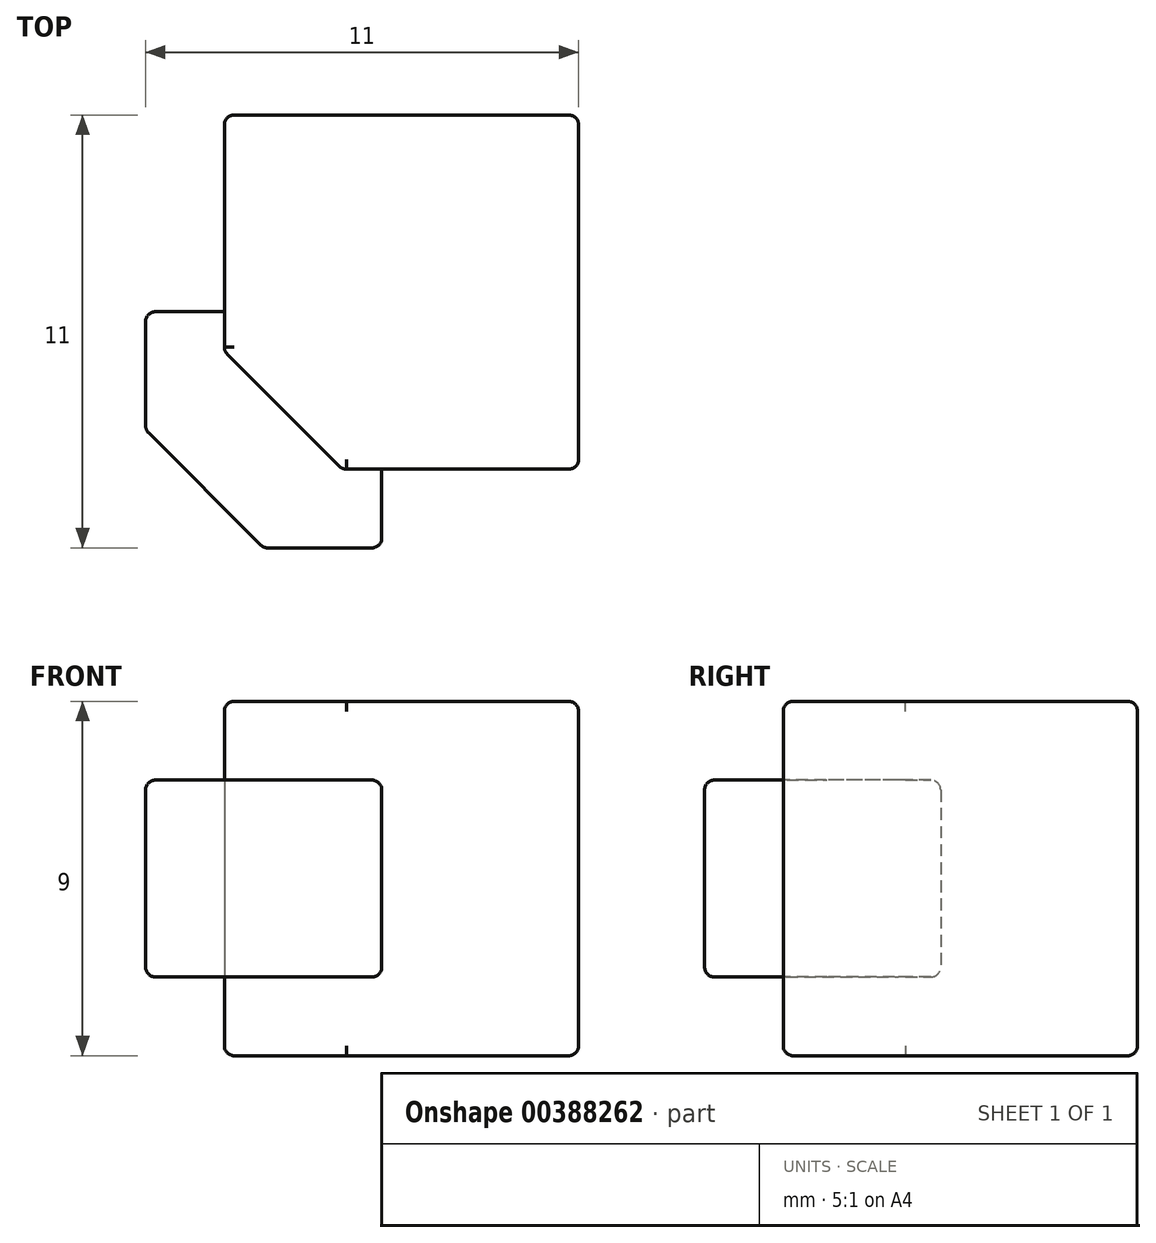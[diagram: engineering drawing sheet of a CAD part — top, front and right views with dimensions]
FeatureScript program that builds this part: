
annotation { "Feature Type Name" : "Feature", "Feature Type Description" : "" }
export const myFeature = defineFeature(function(context is Context, id is Id, definition is map)
    precondition{}
    {
        {
            var Q0;
            Q0=qCreatedBy(makeId("Top.planeOp"),FACE);
            var sketch = newSketch(context, id + "F0", { "sketchPlane" : qUnion([Q0])});
            skLineSegment(sketch, "E0.bottom", {"start": v(4.5, -4.5) * mm, "end": v(-4.5, -4.5) * mm});
            skLineSegment(sketch, "E0.top", {"start": v(4.5, 4.5) * mm, "end": v(-4.5, 4.5) * mm});
            skLineSegment(sketch, "E0.left", {"start": v(4.5, -4.5) * mm, "end": v(4.5, 4.5) * mm});
            skLineSegment(sketch, "E0.right", {"start": v(-4.5, -4.5) * mm, "end": v(-4.5, 4.5) * mm});
            skPoint(sketch, "E0.middle", {"position": v(0, 0) * mm});
            skSolve(sketch);
        }
        {
            var Q0;
            Q0 = qSketchRegion(id + "F0", true);
            extrude(context, id + "F1", {"entities" : qUnion([Q0]), "depth" : 9 * mm});
        }
        {
            var Q0;
            Q0=qCreatedBy(makeId("Top.planeOp"),FACE);
            var sketch = newSketch(context, id + "F2", { "sketchPlane" : qUnion([Q0])});
            skLineSegment(sketch, "E1.bottom", {"start": v(-6.5, -0.5) * mm, "end": v(-0.5, -0.5) * mm});
            skLineSegment(sketch, "E1.top", {"start": v(-6.5, -6.5) * mm, "end": v(-0.5, -6.5) * mm});
            skLineSegment(sketch, "E1.left", {"start": v(-6.5, -0.5) * mm, "end": v(-6.5, -6.5) * mm});
            skLineSegment(sketch, "E1.right", {"start": v(-0.5, -0.5) * mm, "end": v(-0.5, -6.5) * mm});
            skSolve(sketch);
        }
        {
            var Q0;
            Q0=makeQuery(id+"F2.imprint","IMPRINT",FACE,{"disambiguationData":[TD([[makeQuery(id+"F2.imprint","IMPRINT",EDGE,{"derivedFrom":sQuery(id+"F2.wireOp",EDGE,"E1.bottom")}),-1.0]])]});
            extrude(context, id + "F3", {"entities" : qUnion([Q0]), "operationType" : NewBodyOperationType.ADD, "depth" : 7 * mm, "hasSecondDirection" : true, "secondDirectionOppositeDirection" : false, "secondDirectionDepth" : 2 * mm});
        }
        {
            var Q0;
            {var subQ0=sQuery(id+"F0.wireOp",EDGE,"E0.bottom");var subQ1=sQuery(id+"F0.wireOp",EDGE,"E0.right");Q0=makeQuery(id+"F3.boolean.opBoolean","SPLIT",EDGE,{"disambiguationData":[TD([makeQuery(id+"F1.opExtrude","CAP_FACE",FACE,{"disambiguationData":[OSD([subQ0,sQuery(id+"F0.wireOp",EDGE,"E0.top"),sQuery(id+"F0.wireOp",EDGE,"E0.left"),subQ1])],"isStart":true})])],"derivedFrom":makeQuery(id+"F1.opExtrude","SWEPT_EDGE",EDGE,{"disambiguationData":[OSD([subQ0,subQ1])]})});}
            chamfer(context, id + "F4", {"entities" : qUnion([Q0]), "width" : 3 * mm, "tangentPropagation" : true});
        }
        {
            var Q0;
            Q0=makeQuery(id+"F3.opExtrude","SWEPT_EDGE",EDGE,{"disambiguationData":[OSD([sQuery(id+"F2.wireOp",EDGE,"E1.top"),sQuery(id+"F2.wireOp",EDGE,"E1.left")])]});
            chamfer(context, id + "F5", {"entities" : qUnion([Q0]), "width" : 3 * mm, "tangentPropagation" : true});
        }
        {
            var Q0;
            {var subQ0=sQuery(id+"F0.wireOp",EDGE,"E0.bottom");var subQ1=sQuery(id+"F0.wireOp",EDGE,"E0.right");Q0=makeQuery(id+"F3.boolean.opBoolean","SPLIT",EDGE,{"disambiguationData":[TD([makeQuery(id+"F1.opExtrude","CAP_FACE",FACE,{"disambiguationData":[OSD([subQ0,sQuery(id+"F0.wireOp",EDGE,"E0.top"),sQuery(id+"F0.wireOp",EDGE,"E0.left"),subQ1])],"isStart":false})])],"derivedFrom":makeQuery(id+"F1.opExtrude","SWEPT_EDGE",EDGE,{"disambiguationData":[OSD([subQ0,subQ1])]})});}
            chamfer(context, id + "F6", {"entities" : qUnion([Q0]), "width" : 3 * mm, "tangentPropagation" : true});
        }
        {
            var Q0;
            Q0=makeQuery(id+"F1.opExtrude","CAP_EDGE",EDGE,{"disambiguationData":[OSD([sQuery(id+"F0.wireOp",EDGE,"E0.right")])],"isStart":false});
            var Q1;
            Q1=makeQuery(id+"F1.opExtrude","CAP_EDGE",EDGE,{"disambiguationData":[OSD([sQuery(id+"F0.wireOp",EDGE,"E0.top")])],"isStart":false});
            var Q2;
            Q2=makeQuery(id+"F1.opExtrude","CAP_EDGE",EDGE,{"disambiguationData":[OSD([sQuery(id+"F0.wireOp",EDGE,"E0.left")])],"isStart":false});
            var Q3;
            Q3=makeQuery(id+"F1.opExtrude","CAP_EDGE",EDGE,{"disambiguationData":[OSD([sQuery(id+"F0.wireOp",EDGE,"E0.bottom")])],"isStart":false});
            var Q4;
            Q4=makeQuery(id+"F1.opExtrude","SWEPT_EDGE",EDGE,{"disambiguationData":[OSD([sQuery(id+"F0.wireOp",EDGE,"E0.top"),sQuery(id+"F0.wireOp",EDGE,"E0.right")])]});
            var Q5;
            Q5=makeQuery(id+"F1.opExtrude","CAP_EDGE",EDGE,{"disambiguationData":[OSD([sQuery(id+"F0.wireOp",EDGE,"E0.top")])],"isStart":true});
            var Q6;
            Q6=makeQuery(id+"F1.opExtrude","SWEPT_EDGE",EDGE,{"disambiguationData":[OSD([sQuery(id+"F0.wireOp",EDGE,"E0.top"),sQuery(id+"F0.wireOp",EDGE,"E0.left")])]});
            var Q7;
            Q7=makeQuery(id+"F1.opExtrude","CAP_EDGE",EDGE,{"disambiguationData":[OSD([sQuery(id+"F0.wireOp",EDGE,"E0.left")])],"isStart":true});
            var Q8;
            Q8=makeQuery(id+"F1.opExtrude","SWEPT_EDGE",EDGE,{"disambiguationData":[OSD([sQuery(id+"F0.wireOp",EDGE,"E0.bottom"),sQuery(id+"F0.wireOp",EDGE,"E0.left")])]});
            var Q9;
            Q9=makeQuery(id+"F1.opExtrude","CAP_EDGE",EDGE,{"disambiguationData":[OSD([sQuery(id+"F0.wireOp",EDGE,"E0.bottom")])],"isStart":true});
            var Q10;
            Q10=makeQuery(id+"F1.opExtrude","CAP_EDGE",EDGE,{"disambiguationData":[OSD([sQuery(id+"F0.wireOp",EDGE,"E0.right")])],"isStart":true});
            fillet(context, id + "F7", {"entities" : qUnion([Q0, Q1, Q2, Q3, Q4, Q5, Q6, Q7, Q8, Q9, Q10]), "radius" : 0.25 * mm, "tangentPropagation" : true, "allowEdgeOverflow" : false});
        }
        {
            var Q0;
            {var subQ0=sQuery(id+"F0.wireOp",EDGE,"E0.right");var subQ1=sQuery(id+"F0.wireOp",EDGE,"E0.bottom");var subQ2=makeQuery(id+"F1.opExtrude","CAP_FACE",FACE,{"disambiguationData":[OSD([subQ1,sQuery(id+"F0.wireOp",EDGE,"E0.top"),sQuery(id+"F0.wireOp",EDGE,"E0.left"),subQ0])],"isStart":true});Q0=makeQuery(id+"F4.opChamfer","BLEND_EDGE",EDGE,{"blendedFrom":[makeQuery(id+"F3.boolean.opBoolean","SPLIT",EDGE,{"disambiguationData":[TD([subQ2])],"derivedFrom":makeQuery(id+"F1.opExtrude","SWEPT_EDGE",EDGE,{"disambiguationData":[OSD([subQ1,subQ0])]})}),subQ2],"blendedInto":[subQ2]});}
            var Q1;
            {var subQ0=sQuery(id+"F0.wireOp",EDGE,"E0.right");var subQ1=makeQuery(id+"F1.opExtrude","SWEPT_FACE",FACE,{"disambiguationData":[OSD([subQ0])]});var subQ2=sQuery(id+"F0.wireOp",EDGE,"E0.bottom");Q1=makeQuery(id+"F4.opChamfer","BLEND_EDGE",EDGE,{"blendedFrom":[makeQuery(id+"F3.boolean.opBoolean","SPLIT",EDGE,{"disambiguationData":[TD([makeQuery(id+"F1.opExtrude","CAP_FACE",FACE,{"disambiguationData":[OSD([subQ2,sQuery(id+"F0.wireOp",EDGE,"E0.top"),sQuery(id+"F0.wireOp",EDGE,"E0.left"),subQ0])],"isStart":true})])],"derivedFrom":makeQuery(id+"F1.opExtrude","SWEPT_EDGE",EDGE,{"disambiguationData":[OSD([subQ2,subQ0])]})}),subQ1],"blendedInto":[subQ1]});}
            var Q2;
            {var subQ0=sQuery(id+"F0.wireOp",EDGE,"E0.bottom");var subQ1=makeQuery(id+"F1.opExtrude","SWEPT_FACE",FACE,{"disambiguationData":[OSD([subQ0])]});var subQ2=sQuery(id+"F0.wireOp",EDGE,"E0.right");Q2=makeQuery(id+"F4.opChamfer","BLEND_EDGE",EDGE,{"blendedFrom":[makeQuery(id+"F3.boolean.opBoolean","SPLIT",EDGE,{"disambiguationData":[TD([makeQuery(id+"F1.opExtrude","CAP_FACE",FACE,{"disambiguationData":[OSD([subQ0,sQuery(id+"F0.wireOp",EDGE,"E0.top"),sQuery(id+"F0.wireOp",EDGE,"E0.left"),subQ2])],"isStart":true})])],"derivedFrom":makeQuery(id+"F1.opExtrude","SWEPT_EDGE",EDGE,{"disambiguationData":[OSD([subQ0,subQ2])]})}),subQ1],"blendedInto":[subQ1]});}
            var Q3;
            {var subQ0=sQuery(id+"F0.wireOp",EDGE,"E0.right");var subQ1=makeQuery(id+"F1.opExtrude","SWEPT_FACE",FACE,{"disambiguationData":[OSD([subQ0])]});var subQ2=sQuery(id+"F0.wireOp",EDGE,"E0.bottom");Q3=makeQuery(id+"F6.opChamfer","BLEND_EDGE",EDGE,{"blendedFrom":[makeQuery(id+"F3.boolean.opBoolean","SPLIT",EDGE,{"disambiguationData":[TD([makeQuery(id+"F1.opExtrude","CAP_FACE",FACE,{"disambiguationData":[OSD([subQ2,sQuery(id+"F0.wireOp",EDGE,"E0.top"),sQuery(id+"F0.wireOp",EDGE,"E0.left"),subQ0])],"isStart":false})])],"derivedFrom":makeQuery(id+"F1.opExtrude","SWEPT_EDGE",EDGE,{"disambiguationData":[OSD([subQ2,subQ0])]})}),subQ1],"blendedInto":[subQ1]});}
            var Q4;
            {var subQ0=sQuery(id+"F0.wireOp",EDGE,"E0.right");var subQ1=sQuery(id+"F0.wireOp",EDGE,"E0.bottom");var subQ2=makeQuery(id+"F1.opExtrude","CAP_FACE",FACE,{"disambiguationData":[OSD([subQ1,sQuery(id+"F0.wireOp",EDGE,"E0.top"),sQuery(id+"F0.wireOp",EDGE,"E0.left"),subQ0])],"isStart":false});Q4=makeQuery(id+"F6.opChamfer","BLEND_EDGE",EDGE,{"blendedFrom":[makeQuery(id+"F3.boolean.opBoolean","SPLIT",EDGE,{"disambiguationData":[TD([subQ2])],"derivedFrom":makeQuery(id+"F1.opExtrude","SWEPT_EDGE",EDGE,{"disambiguationData":[OSD([subQ1,subQ0])]})}),subQ2],"blendedInto":[subQ2]});}
            var Q5;
            {var subQ0=sQuery(id+"F0.wireOp",EDGE,"E0.bottom");var subQ1=makeQuery(id+"F1.opExtrude","SWEPT_FACE",FACE,{"disambiguationData":[OSD([subQ0])]});var subQ2=sQuery(id+"F0.wireOp",EDGE,"E0.right");Q5=makeQuery(id+"F6.opChamfer","BLEND_EDGE",EDGE,{"blendedFrom":[makeQuery(id+"F3.boolean.opBoolean","SPLIT",EDGE,{"disambiguationData":[TD([makeQuery(id+"F1.opExtrude","CAP_FACE",FACE,{"disambiguationData":[OSD([subQ0,sQuery(id+"F0.wireOp",EDGE,"E0.top"),sQuery(id+"F0.wireOp",EDGE,"E0.left"),subQ2])],"isStart":false})])],"derivedFrom":makeQuery(id+"F1.opExtrude","SWEPT_EDGE",EDGE,{"disambiguationData":[OSD([subQ0,subQ2])]})}),subQ1],"blendedInto":[subQ1]});}
            fillet(context, id + "F8", {"entities" : qUnion([Q0, Q1, Q2, Q3, Q4, Q5]), "radius" : 0.25 * mm, "tangentPropagation" : true, "allowEdgeOverflow" : false});
        }
        {
            var Q0;
            Q0=makeQuery(id+"F3.opExtrude","SWEPT_EDGE",EDGE,{"disambiguationData":[OSD([sQuery(id+"F2.wireOp",EDGE,"E1.top"),sQuery(id+"F2.wireOp",EDGE,"E1.right")])]});
            var Q1;
            Q1=makeQuery(id+"F3.opExtrude","CAP_EDGE",EDGE,{"disambiguationData":[OSD([sQuery(id+"F2.wireOp",EDGE,"E1.right")])],"isStart":false});
            var Q2;
            Q2=makeQuery(id+"F3.opExtrude","CAP_EDGE",EDGE,{"disambiguationData":[OSD([sQuery(id+"F2.wireOp",EDGE,"E1.right")])],"isStart":true});
            var Q3;
            Q3=makeQuery(id+"F3.opExtrude","CAP_EDGE",EDGE,{"disambiguationData":[OSD([sQuery(id+"F2.wireOp",EDGE,"E1.top")])],"isStart":true});
            var Q4;
            Q4=makeQuery(id+"F3.opExtrude","CAP_EDGE",EDGE,{"disambiguationData":[OSD([sQuery(id+"F2.wireOp",EDGE,"E1.top")])],"isStart":false});
            var Q5;
            {var subQ0=sQuery(id+"F2.wireOp",EDGE,"E1.top");Q5=makeQuery(id+"F5.opChamfer","BLEND_EDGE",EDGE,{"blendedFrom":[makeQuery(id+"F3.opExtrude","SWEPT_EDGE",EDGE,{"disambiguationData":[OSD([subQ0,sQuery(id+"F2.wireOp",EDGE,"E1.left")])]}),makeQuery(id+"F3.opExtrude","SWEPT_FACE",FACE,{"disambiguationData":[OSD([subQ0])]})],"blendedInto":[makeQuery(id+"F3.opExtrude","SWEPT_FACE",FACE,{"disambiguationData":[OSD([subQ0])]})]});}
            var Q6;
            {var subQ0=sQuery(id+"F2.wireOp",EDGE,"E1.left");var subQ1=sQuery(id+"F2.wireOp",EDGE,"E1.top");Q6=makeQuery(id+"F5.opChamfer","BLEND_EDGE",EDGE,{"blendedFrom":[makeQuery(id+"F3.opExtrude","SWEPT_EDGE",EDGE,{"disambiguationData":[OSD([subQ1,subQ0])]}),makeQuery(id+"F3.opExtrude","CAP_FACE",FACE,{"disambiguationData":[OSD([sQuery(id+"F2.wireOp",EDGE,"E1.bottom"),subQ1,subQ0,sQuery(id+"F2.wireOp",EDGE,"E1.right")])],"isStart":false})],"blendedInto":[makeQuery(id+"F3.opExtrude","CAP_FACE",FACE,{"disambiguationData":[OSD([sQuery(id+"F2.wireOp",EDGE,"E1.bottom"),subQ1,subQ0,sQuery(id+"F2.wireOp",EDGE,"E1.right")])],"isStart":false})]});}
            var Q7;
            {var subQ0=sQuery(id+"F2.wireOp",EDGE,"E1.left");var subQ1=sQuery(id+"F2.wireOp",EDGE,"E1.top");Q7=makeQuery(id+"F5.opChamfer","BLEND_EDGE",EDGE,{"blendedFrom":[makeQuery(id+"F3.opExtrude","SWEPT_EDGE",EDGE,{"disambiguationData":[OSD([subQ1,subQ0])]}),makeQuery(id+"F3.opExtrude","CAP_FACE",FACE,{"disambiguationData":[OSD([sQuery(id+"F2.wireOp",EDGE,"E1.bottom"),subQ1,subQ0,sQuery(id+"F2.wireOp",EDGE,"E1.right")])],"isStart":true})],"blendedInto":[makeQuery(id+"F3.opExtrude","CAP_FACE",FACE,{"disambiguationData":[OSD([sQuery(id+"F2.wireOp",EDGE,"E1.bottom"),subQ1,subQ0,sQuery(id+"F2.wireOp",EDGE,"E1.right")])],"isStart":true})]});}
            var Q8;
            {var subQ0=sQuery(id+"F2.wireOp",EDGE,"E1.left");Q8=makeQuery(id+"F5.opChamfer","BLEND_EDGE",EDGE,{"blendedFrom":[makeQuery(id+"F3.opExtrude","SWEPT_EDGE",EDGE,{"disambiguationData":[OSD([sQuery(id+"F2.wireOp",EDGE,"E1.top"),subQ0])]}),makeQuery(id+"F3.opExtrude","SWEPT_FACE",FACE,{"disambiguationData":[OSD([subQ0])]})],"blendedInto":[makeQuery(id+"F3.opExtrude","SWEPT_FACE",FACE,{"disambiguationData":[OSD([subQ0])]})]});}
            var Q9;
            Q9=makeQuery(id+"F3.opExtrude","CAP_EDGE",EDGE,{"disambiguationData":[OSD([sQuery(id+"F2.wireOp",EDGE,"E1.left")])],"isStart":false});
            var Q10;
            Q10=makeQuery(id+"F3.opExtrude","SWEPT_EDGE",EDGE,{"disambiguationData":[OSD([sQuery(id+"F2.wireOp",EDGE,"E1.bottom"),sQuery(id+"F2.wireOp",EDGE,"E1.left")])]});
            var Q11;
            Q11=makeQuery(id+"F3.opExtrude","CAP_EDGE",EDGE,{"disambiguationData":[OSD([sQuery(id+"F2.wireOp",EDGE,"E1.left")])],"isStart":true});
            var Q12;
            Q12=makeQuery(id+"F3.opExtrude","CAP_EDGE",EDGE,{"disambiguationData":[OSD([sQuery(id+"F2.wireOp",EDGE,"E1.bottom")])],"isStart":true});
            var Q13;
            Q13=makeQuery(id+"F3.opExtrude","CAP_EDGE",EDGE,{"disambiguationData":[OSD([sQuery(id+"F2.wireOp",EDGE,"E1.bottom")])],"isStart":false});
            fillet(context, id + "F9", {"entities" : qUnion([Q0, Q1, Q2, Q3, Q4, Q5, Q6, Q7, Q8, Q9, Q10, Q11, Q12, Q13]), "radius" : 0.25 * mm, "tangentPropagation" : true, "allowEdgeOverflow" : false});
        }
    });
